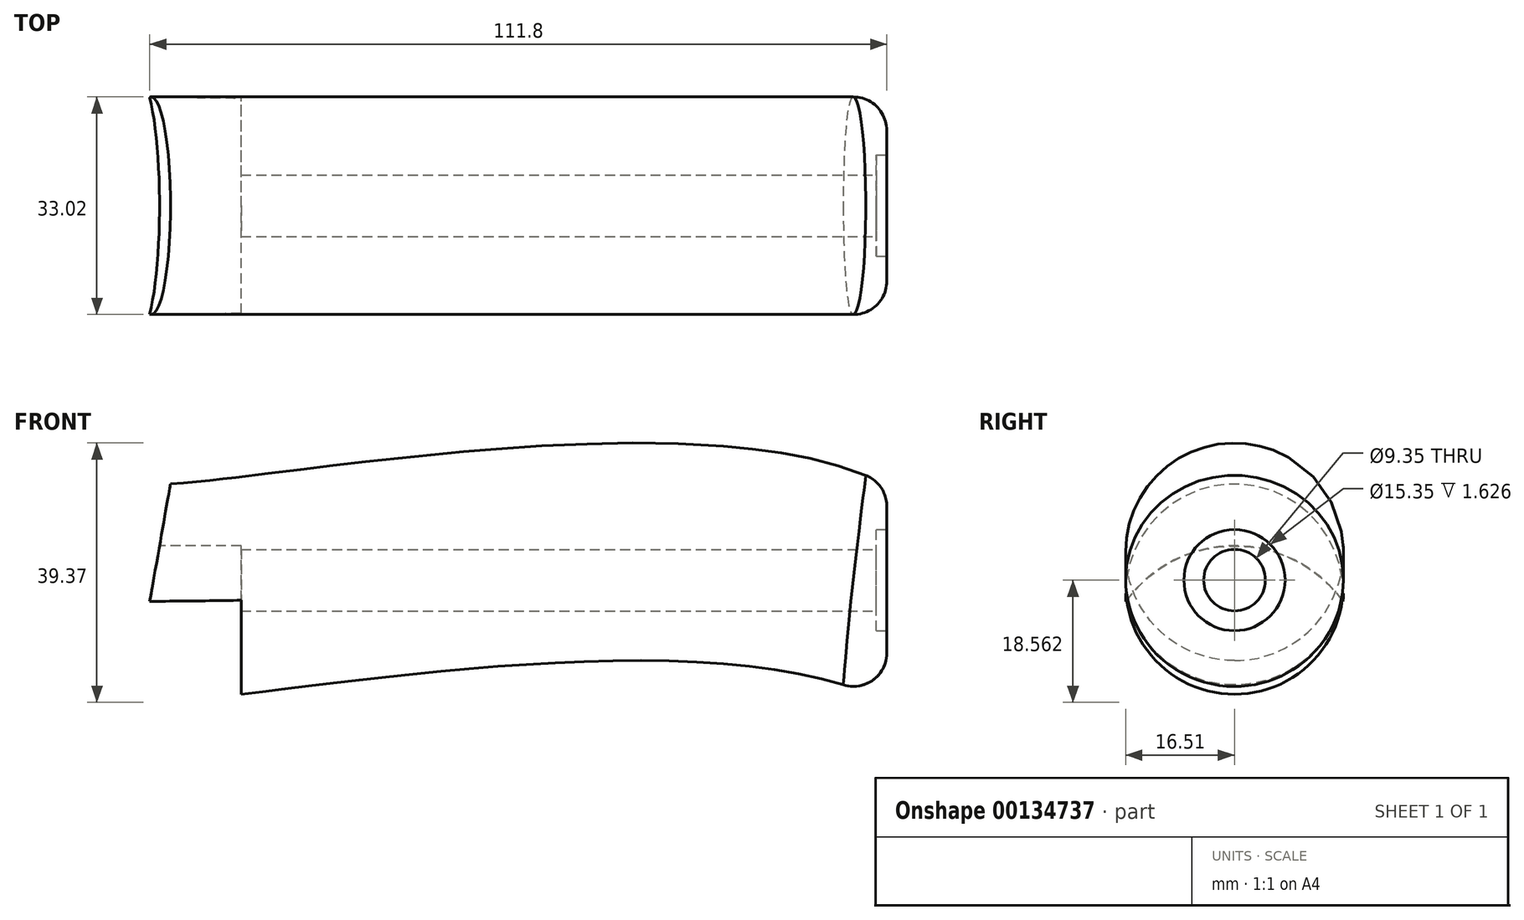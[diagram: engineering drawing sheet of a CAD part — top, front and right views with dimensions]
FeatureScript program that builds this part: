
annotation { "Feature Type Name" : "Feature", "Feature Type Description" : "" }
export const myFeature = defineFeature(function(context is Context, id is Id, definition is map)
    precondition{}
    {
        {
            var Q0;
            Q0=qCreatedBy(makeId("Front.planeOp"),FACE);
            var sketch = newSketch(context, id + "F0", { "sketchPlane" : qUnion([Q0])});
            skFitSpline(sketch, "E0", {"points": [v(-56.03, 0) * mm, v(55.88, 0) * mm], "startDerivative": vector(47.94, 0) * mm, "endDerivative": vector(83.13, -42.83) * mm});
            skSolve(sketch);
        }
        {
            var Q0;
            Q0=qCreatedBy(makeId("Right.planeOp"),FACE);
            cPlane(context, id + "F1", {"entities" : qUnion([Q0]), "cplaneType" : CPlaneType.OFFSET, "offset" : 55.88 * mm, "width" : 152.4 * mm, "height" : 152.4 * mm});
        }
        {
            var Q0;
            Q0=qCreatedBy(id+"F1.planeOp",FACE);
            var sketch = newSketch(context, id + "F2", { "sketchPlane" : qUnion([Q0])});
            skCircle(sketch, "E1", {"center": v(0, 0) * mm, "radius": 4.76 * mm, "construction": true});
            skCircle(sketch, "E2", {"center": v(0, 2.46) * mm, "radius": 16.51 * mm});
            skSolve(sketch);
        }
        {
            var Q0;
            Q0 = qSketchRegion(id + "F2", true);
            var Q1;
            Q1 = qConstructionFilter(qBodyType(qCreatedBy(id + "F0" ,EDGE), BodyType.WIRE), ConstructionObject.NO);
            sweep(context, id + "F3", {"profiles" : qUnion([Q0]), "path" : qUnion([Q1]), "keepProfileOrientation" : true});
        }
        {
            var Q0;
            Q0=makeQuery(id+"F3.opSweep","CAP_EDGE",EDGE,{"disambiguationData":[OSD([sQuery(id+"F0.wireOp",VERTEX,"E0.end"),sQuery(id+"F2.wireOp",EDGE,"E2")])],"isStart":true});
            fillet(context, id + "F4", {"entities" : qUnion([Q0]), "radius" : 5.08 * mm, "tangentPropagation" : true, "allowEdgeOverflow" : false});
        }
        {
            var Q0;
            Q0=makeQuery(id+"F3.opSweep","CAP_FACE",FACE,{"disambiguationData":[OSD([sQuery(id+"F0.wireOp",VERTEX,"E0.start"),sQuery(id+"F2.wireOp",EDGE,"E1"),sQuery(id+"F2.wireOp",EDGE,"E2")])],"isStart":false});
            var sketch = newSketch(context, id + "F5", { "sketchPlane" : qUnion([Q0])});
            skArc(sketch, "E3", {"start": v(16.47, 1.3) * mm, "mid": v(0, 9.73) * mm, "end": v(-16.47, 1.3) * mm});
            skArc(sketch, "E4", {"start": v(-16.47, 1.3) * mm, "mid": v(0, -14.05) * mm, "end": v(16.47, 1.3) * mm});
            skSolve(sketch);
        }
        {
            var Q0;
            Q0 = qSketchRegion(id + "F5", true);
            extrude(context, id + "F6", {"entities" : qUnion([Q0]), "operationType" : NewBodyOperationType.REMOVE, "oppositeDirection" : true, "depth" : 13.97 * mm});
        }
        {
            var Q0;
            Q0=makeQuery(id+"F3.opSweep","CAP_FACE",FACE,{"disambiguationData":[OSD([sQuery(id+"F0.wireOp",VERTEX,"E0.end"),sQuery(id+"F2.wireOp",EDGE,"E2")])],"isStart":true});
            var sketch = newSketch(context, id + "F7", { "sketchPlane" : qUnion([Q0])});
            skLineSegment(sketch, "E5", {"start": v(-11.43, 4.51) * mm, "end": v(11.43, 4.51) * mm, "construction": true});
            skLineSegment(sketch, "E6", {"start": v(0, 15.7) * mm, "end": v(0, -6.54) * mm, "construction": true});
            skPoint(sketch, "E7", {"position": v(0, 4.51) * mm});
            skSolve(sketch);
        }
        {
            var Q0;
            Q0=sQuery(id+"F7.wireOp",VERTEX,"E7");
            var Q1;
            Q1=makeQuery(id+"F3.opSweep","SWEPT_BODY",BODY,{"disambiguationData":[OSD([sQuery(id+"F0.wireOp",EDGE,"E0"),sQuery(id+"F2.wireOp",EDGE,"E2")])]});
            hole(context, id + "F8", {"style" : HoleStyle.C_BORE, "endStyle" : HoleEndStyle.THROUGH, "holeDiameter" : 9.35 * mm, "cBoreDiameter" : 15.35 * mm, "cBoreDepth" : 1.63 * mm, "startFromSketch" : true, "locations" : qUnion([Q0]), "scope" : qUnion([Q1]), "isTappedThrough" : true});
        }
        {
            var Q0;
            Q0=qCreatedBy(makeId("Front.planeOp"),FACE);
            var sketch = newSketch(context, id + "F9", { "sketchPlane" : qUnion([Q0])});
            skLineSegment(sketch, "E8", {"start": v(-56.15, 0) * mm, "end": v(-48.8, 41.7) * mm});
            skLineSegment(sketch, "E9", {"start": v(-56.15, 0) * mm, "end": v(-56.15, 41.7) * mm});
            skLineSegment(sketch, "E10", {"start": v(-48.8, 41.7) * mm, "end": v(-56.15, 41.7) * mm});
            skSolve(sketch);
        }
        {
            var Q0;
            Q0 = qSketchRegion(id + "F9", true);
            extrude(context, id + "F10", {"entities" : qUnion([Q0]), "operationType" : NewBodyOperationType.REMOVE, "depth" : 127 * mm, "hasSecondDirection" : true, "secondDirectionOppositeDirection" : true, "secondDirectionDepth" : 127 * mm});
        }
    });
